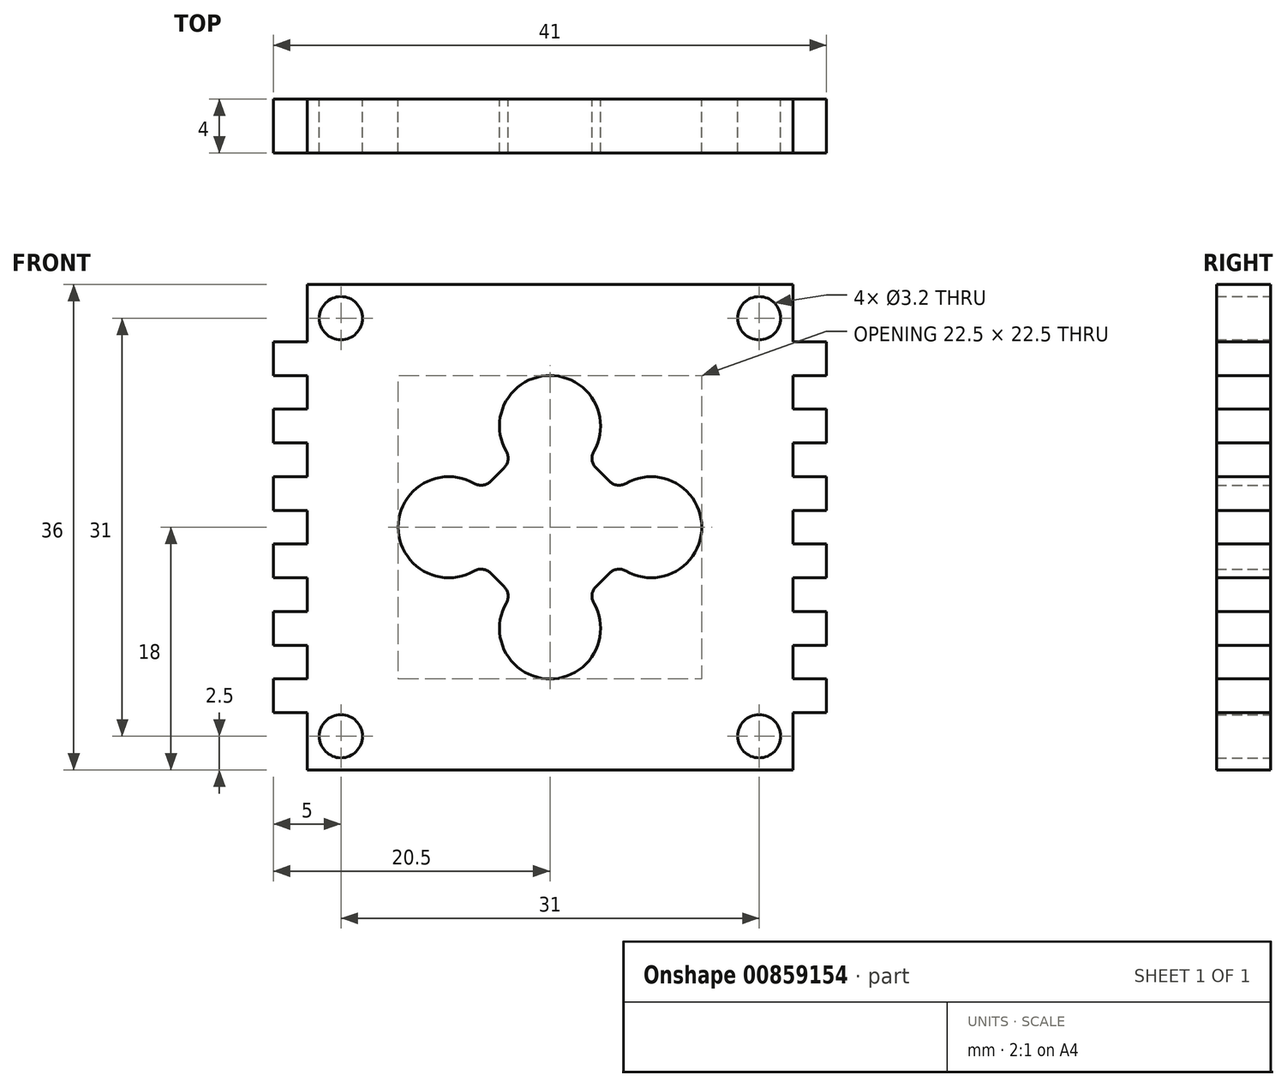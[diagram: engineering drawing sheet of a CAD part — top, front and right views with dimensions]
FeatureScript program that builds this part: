
annotation { "Feature Type Name" : "Feature", "Feature Type Description" : "" }
export const myFeature = defineFeature(function(context is Context, id is Id, definition is map)
    precondition{}
    {
        {
            var Q0;
            Q0=qCreatedBy(makeId("Front.planeOp"),FACE);
            var sketch = newSketch(context, id + "F0", { "sketchPlane" : qUnion([Q0])});
            skLineSegment(sketch, "E0.bottom", {"start": v(-18, 18) * mm, "end": v(18, 18) * mm});
            skLineSegment(sketch, "E0.top", {"start": v(-18, -18) * mm, "end": v(18, -18) * mm});
            skLineSegment(sketch, "E0.left", {"start": v(-18, 18) * mm, "end": v(-18, 13.75) * mm});
            skLineSegment(sketch, "E0.right", {"start": v(18, 18) * mm, "end": v(18, 13.75) * mm});
            skCircle(sketch, "E1", {"center": v(-15.5, 15.5) * mm, "radius": 1.6 * mm});
            skLineSegment(sketch, "E2", {"start": v(0, 24.04) * mm, "end": v(0, -29.5) * mm, "construction": true});
            skLineSegment(sketch, "E3", {"start": v(-31.46, 0) * mm, "end": v(29.02, 0) * mm, "construction": true});
            skCircle(sketch, "E4.MirrorC", {"center": v(15.5, 15.5) * mm, "radius": 1.6 * mm});
            skCircle(sketch, "E5.MirrorC", {"center": v(-15.5, -15.5) * mm, "radius": 1.6 * mm});
            skCircle(sketch, "E6.MirrorC", {"center": v(15.5, -15.5) * mm, "radius": 1.6 * mm});
            skLineSegment(sketch, "E7", {"start": v(18, 13.75) * mm, "end": v(20.5, 13.75) * mm});
            skLineSegment(sketch, "E8", {"start": v(20.5, 13.75) * mm, "end": v(20.5, 11.25) * mm});
            skLineSegment(sketch, "E9", {"start": v(20.5, 11.25) * mm, "end": v(18, 11.25) * mm});
            skLineSegment(sketch, "E10", {"start": v(18, 8.75) * mm, "end": v(20.5, 8.75) * mm});
            skLineSegment(sketch, "E11", {"start": v(20.5, 8.75) * mm, "end": v(20.5, 6.25) * mm});
            skLineSegment(sketch, "E12", {"start": v(20.5, 6.25) * mm, "end": v(18, 6.25) * mm});
            skLineSegment(sketch, "E13", {"start": v(18, 3.75) * mm, "end": v(20.5, 3.75) * mm});
            skLineSegment(sketch, "E14", {"start": v(20.5, 3.75) * mm, "end": v(20.5, 1.25) * mm});
            skLineSegment(sketch, "E15", {"start": v(20.5, 1.25) * mm, "end": v(18, 1.25) * mm});
            skLineSegment(sketch, "E16.trimOffspring", {"start": v(18, 11.25) * mm, "end": v(18, 8.75) * mm});
            skLineSegment(sketch, "E17.trimOffspring", {"start": v(18, 6.25) * mm, "end": v(18, 3.75) * mm});
            skLineSegment(sketch, "E18.trimOffspring", {"start": v(18, 1.25) * mm, "end": v(18, -1.25) * mm});
            skLineSegment(sketch, "E19.MirrorCS", {"start": v(-20.5, 3.75) * mm, "end": v(-20.5, 1.25) * mm});
            skLineSegment(sketch, "E20.MirrorCS", {"start": v(-20.5, 13.75) * mm, "end": v(-20.5, 11.25) * mm});
            skLineSegment(sketch, "E21.MirrorCS", {"start": v(-18, 11.25) * mm, "end": v(-18, 8.75) * mm});
            skLineSegment(sketch, "E22.MirrorCS", {"start": v(-18, 6.25) * mm, "end": v(-18, 3.75) * mm});
            skLineSegment(sketch, "E23.MirrorCS", {"start": v(-20.5, 1.25) * mm, "end": v(-18, 1.25) * mm});
            skLineSegment(sketch, "E24.MirrorCS", {"start": v(-18, 8.75) * mm, "end": v(-20.5, 8.75) * mm});
            skLineSegment(sketch, "E25.MirrorCS", {"start": v(-18, 3.75) * mm, "end": v(-20.5, 3.75) * mm});
            skLineSegment(sketch, "E26.MirrorCS", {"start": v(-20.5, 8.75) * mm, "end": v(-20.5, 6.25) * mm});
            skLineSegment(sketch, "E27.MirrorCS", {"start": v(-20.5, 6.25) * mm, "end": v(-18, 6.25) * mm});
            skLineSegment(sketch, "E28.MirrorCS", {"start": v(-20.5, 11.25) * mm, "end": v(-18, 11.25) * mm});
            skLineSegment(sketch, "E29.MirrorCS", {"start": v(-18, 13.75) * mm, "end": v(-20.5, 13.75) * mm});
            skLineSegment(sketch, "E30.MirrorCS", {"start": v(-18, -11.25) * mm, "end": v(-18, -8.75) * mm});
            skLineSegment(sketch, "E31.MirrorCS", {"start": v(-18, -8.75) * mm, "end": v(-20.5, -8.75) * mm});
            skLineSegment(sketch, "E32.MirrorCS", {"start": v(-20.5, -13.75) * mm, "end": v(-20.5, -11.25) * mm});
            skLineSegment(sketch, "E33.MirrorCS", {"start": v(-20.5, -6.25) * mm, "end": v(-18, -6.25) * mm});
            skLineSegment(sketch, "E34.MirrorCS", {"start": v(-20.5, -11.25) * mm, "end": v(-18, -11.25) * mm});
            skLineSegment(sketch, "E35.MirrorCS", {"start": v(-20.5, -8.75) * mm, "end": v(-20.5, -6.25) * mm});
            skLineSegment(sketch, "E36.MirrorCS", {"start": v(-18, -3.75) * mm, "end": v(-20.5, -3.75) * mm});
            skLineSegment(sketch, "E37.MirrorCS", {"start": v(-18, -13.75) * mm, "end": v(-20.5, -13.75) * mm});
            skLineSegment(sketch, "E38.MirrorCS", {"start": v(-20.5, -1.25) * mm, "end": v(-18, -1.25) * mm});
            skLineSegment(sketch, "E39.MirrorCS", {"start": v(-18, -6.25) * mm, "end": v(-18, -3.75) * mm});
            skLineSegment(sketch, "E40.MirrorCS", {"start": v(-20.5, -3.75) * mm, "end": v(-20.5, -1.25) * mm});
            skLineSegment(sketch, "E41.MirrorCS", {"start": v(20.5, -1.25) * mm, "end": v(18, -1.25) * mm});
            skLineSegment(sketch, "E42.MirrorCS", {"start": v(20.5, -3.75) * mm, "end": v(20.5, -1.25) * mm});
            skLineSegment(sketch, "E43.MirrorCS", {"start": v(18, -11.25) * mm, "end": v(18, -8.75) * mm});
            skLineSegment(sketch, "E44.MirrorCS", {"start": v(18, -3.75) * mm, "end": v(20.5, -3.75) * mm});
            skLineSegment(sketch, "E45.MirrorCS", {"start": v(20.5, -6.25) * mm, "end": v(18, -6.25) * mm});
            skLineSegment(sketch, "E46.MirrorCS", {"start": v(18, -6.25) * mm, "end": v(18, -3.75) * mm});
            skLineSegment(sketch, "E47.MirrorCS", {"start": v(20.5, -8.75) * mm, "end": v(20.5, -6.25) * mm});
            skLineSegment(sketch, "E48.MirrorCS", {"start": v(18, -8.75) * mm, "end": v(20.5, -8.75) * mm});
            skLineSegment(sketch, "E49.MirrorCS", {"start": v(20.5, -13.75) * mm, "end": v(20.5, -11.25) * mm});
            skLineSegment(sketch, "E50.MirrorCS", {"start": v(18, -13.75) * mm, "end": v(20.5, -13.75) * mm});
            skLineSegment(sketch, "E51.MirrorCS", {"start": v(20.5, -11.25) * mm, "end": v(18, -11.25) * mm});
            skLineSegment(sketch, "E52.trimOffspring", {"start": v(-18, 1.25) * mm, "end": v(-18, -1.25) * mm});
            skLineSegment(sketch, "E53.trimOffspring", {"start": v(-18, -3.75) * mm, "end": v(-18, -6.25) * mm});
            skLineSegment(sketch, "E54.trimOffspring", {"start": v(-18, -8.75) * mm, "end": v(-18, -11.25) * mm});
            skLineSegment(sketch, "E55.trimOffspring", {"start": v(-18, -13.75) * mm, "end": v(-18, -18) * mm});
            skLineSegment(sketch, "E56.trimOffspring", {"start": v(18, -13.75) * mm, "end": v(18, -18) * mm});
            skLineSegment(sketch, "E57.trimOffspring", {"start": v(18, -8.75) * mm, "end": v(18, -11.25) * mm});
            skLineSegment(sketch, "E58.trimOffspring", {"start": v(18, -3.75) * mm, "end": v(18, -6.25) * mm});
            skArc(sketch, "E59", {"start": v(3.24, 5.62) * mm, "mid": v(0, 11.25) * mm, "end": v(-3.24, 5.62) * mm});
            skArc(sketch, "E60.MirrorC", {"start": v(3.24, -5.62) * mm, "mid": v(0, -11.25) * mm, "end": v(-3.24, -5.62) * mm});
            skArc(sketch, "E61", {"start": v(-5.62, 3.24) * mm, "mid": v(-11.25, 0) * mm, "end": v(-5.62, -3.24) * mm});
            skArc(sketch, "E62.MirrorC", {"start": v(5.62, 3.24) * mm, "mid": v(11.25, 0) * mm, "end": v(5.62, -3.24) * mm});
            skLineSegment(sketch, "E63", {"start": v(-4.4, 3.4) * mm, "end": v(-3.4, 4.4) * mm});
            skLineSegment(sketch, "E64.MirrorCS", {"start": v(4.4, 3.4) * mm, "end": v(3.4, 4.4) * mm});
            skLineSegment(sketch, "E65.MirrorCS", {"start": v(-4.4, -3.4) * mm, "end": v(-3.4, -4.4) * mm});
            skLineSegment(sketch, "E66.MirrorCS", {"start": v(4.4, -3.4) * mm, "end": v(3.4, -4.4) * mm});
            skPoint(sketch, "E67.visualSharp", {"position": v(-5, 2.8) * mm});
            skArc(sketch, "E67.filletArc", {"start": v(-5.15, 2.93) * mm, "mid": v(-5, 2.88) * mm, "end": v(-4.87, 2.94) * mm});
            skArc(sketch, "E68.filletArc", {"start": v(-5.62, 3.24) * mm, "mid": v(-4.99, 3.12) * mm, "end": v(-4.4, 3.4) * mm});
            skPoint(sketch, "E69.visualSharp", {"position": v(-2.8, 5) * mm});
            skArc(sketch, "E69.filletArc", {"start": v(-3.4, 4.4) * mm, "mid": v(-3.12, 4.99) * mm, "end": v(-3.24, 5.62) * mm});
            skPoint(sketch, "E70.visualSharp", {"position": v(2.8, 5) * mm});
            skArc(sketch, "E70.filletArc", {"start": v(3.24, 5.62) * mm, "mid": v(3.12, 4.99) * mm, "end": v(3.4, 4.4) * mm});
            skPoint(sketch, "E71.visualSharp", {"position": v(5, 2.8) * mm});
            skArc(sketch, "E71.filletArc", {"start": v(4.4, 3.4) * mm, "mid": v(4.99, 3.12) * mm, "end": v(5.62, 3.24) * mm});
            skPoint(sketch, "E72.visualSharp", {"position": v(5, -2.8) * mm});
            skArc(sketch, "E72.filletArc", {"start": v(5.62, -3.24) * mm, "mid": v(4.99, -3.12) * mm, "end": v(4.4, -3.4) * mm});
            skPoint(sketch, "E73.visualSharp", {"position": v(2.8, -5) * mm});
            skArc(sketch, "E73.filletArc", {"start": v(3.4, -4.4) * mm, "mid": v(3.12, -4.99) * mm, "end": v(3.24, -5.62) * mm});
            skPoint(sketch, "E74.visualSharp", {"position": v(-5, -2.8) * mm});
            skArc(sketch, "E74.filletArc", {"start": v(-4.4, -3.4) * mm, "mid": v(-4.99, -3.12) * mm, "end": v(-5.62, -3.24) * mm});
            skPoint(sketch, "E75.visualSharp", {"position": v(-2.8, -5) * mm});
            skArc(sketch, "E75.filletArc", {"start": v(-3.24, -5.62) * mm, "mid": v(-3.12, -4.99) * mm, "end": v(-3.4, -4.4) * mm});
            skSolve(sketch);
        }
        {
            var Q0;
            Q0 = qSketchRegion(id + "F0", true);
            extrude(context, id + "F1", {"entities" : qUnion([Q0]), "depth" : 4 * mm, "offsetDistance" : 25 * mm});
        }
    });
